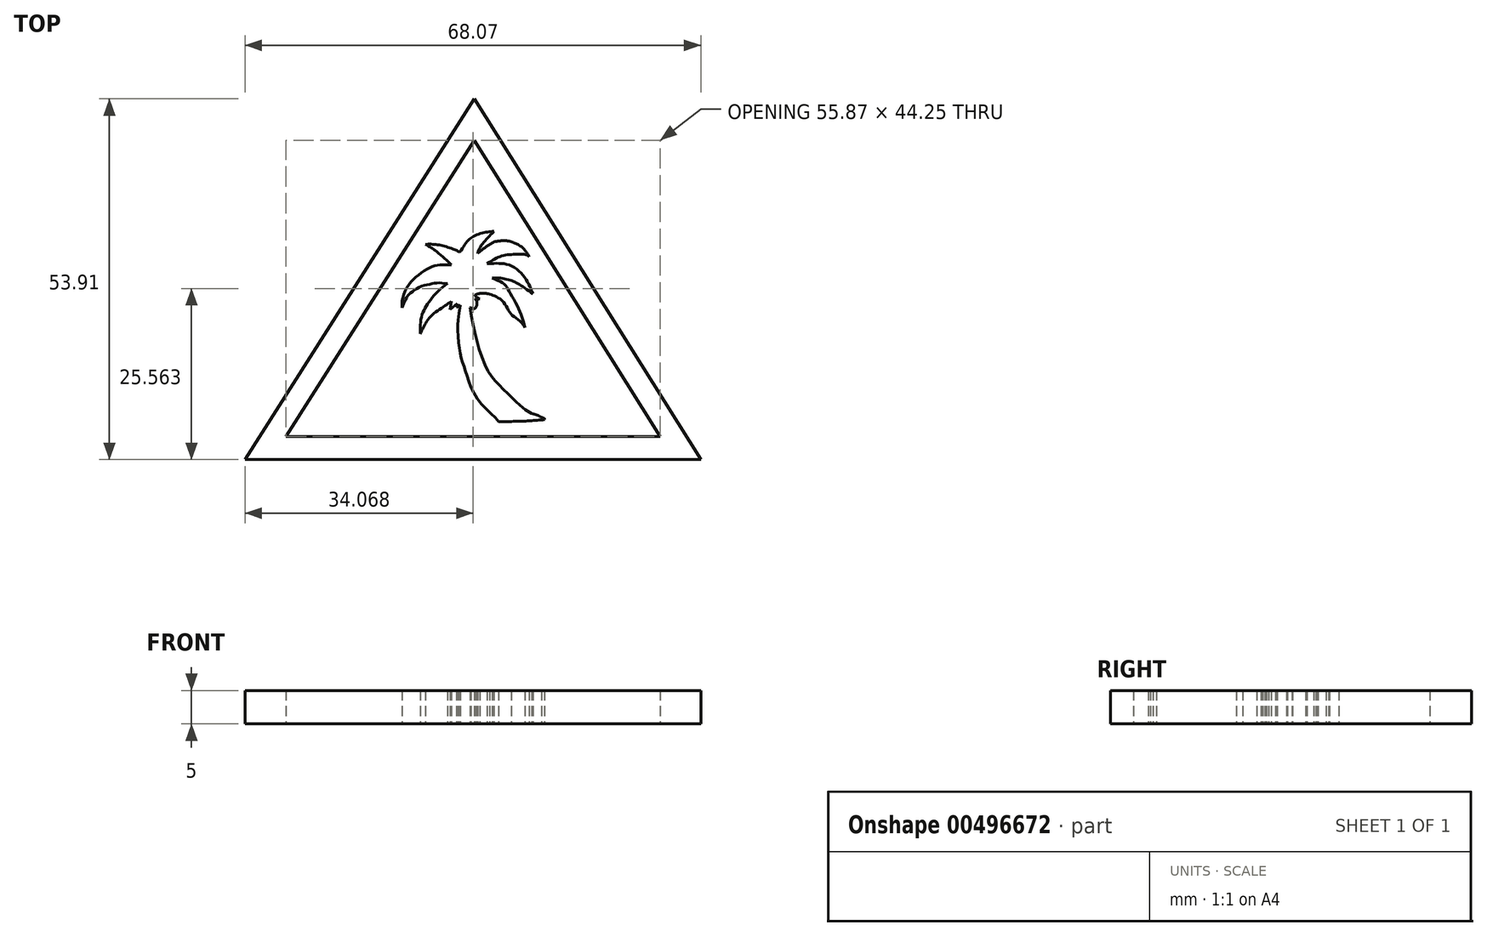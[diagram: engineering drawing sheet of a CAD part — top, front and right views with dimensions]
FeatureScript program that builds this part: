
annotation { "Feature Type Name" : "Feature", "Feature Type Description" : "" }
export const myFeature = defineFeature(function(context is Context, id is Id, definition is map)
    precondition{}
    {
        {
            var Q0;
            Q0=qCreatedBy(makeId("Top.planeOp"),FACE);
            var sketch = newSketch(context, id + "F0", { "sketchPlane" : qUnion([Q0])});
            skLineSegment(sketch, "E0", {"start": v(-38.72, -7.08) * mm, "end": v(-72.96, -61) * mm});
            skLineSegment(sketch, "E1", {"start": v(-72.96, -61) * mm, "end": v(-4.9, -61) * mm});
            skLineSegment(sketch, "E2", {"start": v(-4.9, -61) * mm, "end": v(-38.72, -7.08) * mm});
            skLineSegment(sketch, "E3", {"start": v(-38.72, -13.3) * mm, "end": v(-66.83, -57.55) * mm});
            skLineSegment(sketch, "E4", {"start": v(-66.83, -57.55) * mm, "end": v(-10.96, -57.55) * mm});
            skLineSegment(sketch, "E5", {"start": v(-10.96, -57.55) * mm, "end": v(-38.72, -13.3) * mm});
            skFitSpline(sketch, "E6", {"points": [v(-35.11, -55.3) * mm, v(-31.32, -55.23) * mm, v(-28.22, -55.01) * mm], "startDerivative": vector(7.4, 0.05) * mm, "endDerivative": vector(6.35, 0.54) * mm});
            skFitSpline(sketch, "E7", {"points": [v(-28.22, -55.01) * mm, v(-28.22, -54.88) * mm, v(-28.42, -54.76) * mm, v(-28.66, -54.66) * mm], "startDerivative": vector(0.13, 0.53) * mm, "endDerivative": vector(-0.6, 0.27) * mm});
            skFitSpline(sketch, "E8", {"points": [v(-28.66, -54.66) * mm, v(-29.15, -54.42) * mm, v(-29.59, -54.26) * mm, v(-30.15, -54.1) * mm], "startDerivative": vector(-1.48, 0.76) * mm, "endDerivative": vector(-1.68, 0.48) * mm});
            skFitSpline(sketch, "E9", {"points": [v(-30.15, -54.1) * mm, v(-30.76, -53.73) * mm, v(-31.6, -53.12) * mm, v(-34.28, -50.57) * mm, v(-37.07, -47) * mm, v(-39.14, -39.62) * mm, v(-39.35, -38.29) * mm], "startDerivative": vector(-7.1, 4.24) * mm, "endDerivative": vector(-1.12, 8.32) * mm});
            skFitSpline(sketch, "E10", {"points": [v(-39.35, -38.29) * mm, v(-39.25, -38.22) * mm], "startDerivative": vector(0.1, 0.07) * mm, "endDerivative": vector(0.1, 0.07) * mm});
            skFitSpline(sketch, "E11", {"points": [v(-39.25, -38.22) * mm, v(-39.05, -38.4) * mm, v(-38.8, -38.43) * mm, v(-38.54, -38.29) * mm, v(-38.35, -37.95) * mm, v(-38.33, -37.5) * mm, v(-38.4, -37.24) * mm, v(-38.55, -37.08) * mm, v(-38.55, -37) * mm, v(-38.24, -37) * mm, v(-37.9, -36.97) * mm], "startDerivative": vector(1.92, -2.22) * mm, "endDerivative": vector(2.89, 0.42) * mm});
            skFitSpline(sketch, "E12", {"points": [v(-37.9, -36.97) * mm, v(-38.6, -36.5) * mm, v(-38.62, -36.36) * mm], "startDerivative": vector(-1.33, 0.71) * mm, "endDerivative": vector(0.06, 0.47) * mm});
            skFitSpline(sketch, "E13", {"points": [v(-38.62, -36.36) * mm, v(-38.19, -36.22) * mm, v(-37.53, -36.13) * mm, v(-36.8, -36.18) * mm, v(-36.45, -36.25) * mm], "startDerivative": vector(1.82, 0.64) * mm, "endDerivative": vector(1.56, -0.34) * mm});
            skFitSpline(sketch, "E14", {"points": [v(-36.45, -36.25) * mm, v(-35.77, -36.5) * mm, v(-34.87, -36.98) * mm, v(-34, -37.93) * mm, v(-33.48, -38.95) * mm, v(-32.7, -39.7) * mm, v(-31.68, -40.48) * mm, v(-31.18, -41.25) * mm], "startDerivative": vector(5.54, -2.02) * mm, "endDerivative": vector(3.12, -5.94) * mm});
            skFitSpline(sketch, "E15", {"points": [v(-31.18, -41.25) * mm, v(-31.42, -40.28) * mm, v(-32.26, -38.1) * mm, v(-33.6, -35.68) * mm, v(-34.27, -34.75) * mm, v(-36.05, -33.87) * mm], "startDerivative": vector(-1.3, 5.92) * mm, "endDerivative": vector(-9.79, 3.92) * mm});
            skFitSpline(sketch, "E16", {"points": [v(-36.05, -33.87) * mm, v(-34.72, -33.87) * mm, v(-33.18, -34.24) * mm, v(-32.04, -34.78) * mm, v(-29.98, -36.23) * mm], "startDerivative": vector(5.72, 0.36) * mm, "endDerivative": vector(7.2, -5.3) * mm});
            skFitSpline(sketch, "E17", {"points": [v(-29.98, -36.23) * mm, v(-30.71, -34.56) * mm, v(-31.9, -32.98) * mm, v(-33.61, -31.86) * mm, v(-35.36, -31.66) * mm, v(-36.8, -31.7) * mm], "startDerivative": vector(-3.28, 8.41) * mm, "endDerivative": vector(-7.83, -0.25) * mm});
            skFitSpline(sketch, "E18", {"points": [v(-36.8, -31.7) * mm, v(-35.42, -30.88) * mm, v(-34.16, -30.44) * mm, v(-32.66, -30.31) * mm, v(-31.18, -30.34) * mm, v(-30.52, -30.66) * mm], "startDerivative": vector(6.28, 3.97) * mm, "endDerivative": vector(3.84, -2.53) * mm});
            skFitSpline(sketch, "E19", {"points": [v(-30.52, -30.66) * mm, v(-30.88, -30.06) * mm, v(-31.72, -29.16) * mm, v(-32.79, -28.56) * mm, v(-33.18, -28.44) * mm], "startDerivative": vector(-1.4, 2.53) * mm, "endDerivative": vector(-1.98, 0.53) * mm});
            skFitSpline(sketch, "E20", {"points": [v(-33.18, -28.44) * mm, v(-33.66, -28.31) * mm, v(-34.27, -28.28) * mm, v(-34.8, -28.3) * mm, v(-35.77, -28.44) * mm], "startDerivative": vector(-2.05, 0.68) * mm, "endDerivative": vector(-3.38, -0.57) * mm});
            skFitSpline(sketch, "E21", {"points": [v(-35.77, -28.44) * mm, v(-36.97, -29.2) * mm, v(-38.23, -30.17) * mm], "startDerivative": vector(-2.47, -1.48) * mm, "endDerivative": vector(-2.44, -1.99) * mm});
            skFitSpline(sketch, "E22", {"points": [v(-38.23, -30.17) * mm, v(-37.82, -29.2) * mm, v(-35.77, -26.88) * mm], "startDerivative": vector(0.72, 2.46) * mm, "endDerivative": vector(3.92, 4) * mm});
            skFitSpline(sketch, "E23", {"points": [v(-35.77, -26.88) * mm, v(-37.05, -27.02) * mm, v(-38.6, -27.5) * mm, v(-39.68, -28.3) * mm, v(-40.88, -29.98) * mm], "startDerivative": vector(-5.43, -0.37) * mm, "endDerivative": vector(-4.17, -6.5) * mm});
            skFitSpline(sketch, "E24", {"points": [v(-40.88, -29.98) * mm, v(-41.63, -29.63) * mm, v(-43.15, -29.1) * mm, v(-44.84, -28.82) * mm, v(-46.02, -28.82) * mm], "startDerivative": vector(-3.38, 1.71) * mm, "endDerivative": vector(-4.75, -0.19) * mm});
            skFitSpline(sketch, "E25", {"points": [v(-46.02, -28.82) * mm, v(-44.8, -29.55) * mm, v(-43.82, -30.33) * mm, v(-42.15, -31.86) * mm], "startDerivative": vector(4.1, -2.34) * mm, "endDerivative": vector(4.55, -4.23) * mm});
            skFitSpline(sketch, "E26", {"points": [v(-42.15, -31.86) * mm, v(-43.47, -31.86) * mm, v(-44.58, -32.02) * mm, v(-45.6, -32.43) * mm, v(-47.16, -33.48) * mm, v(-48.46, -34.77) * mm, v(-49.36, -36.6) * mm, v(-49.53, -38.28) * mm], "startDerivative": vector(-10.14, 0.24) * mm, "endDerivative": vector(-0.22, -11.13) * mm});
            skFitSpline(sketch, "E27", {"points": [v(-49.53, -38.28) * mm, v(-49.14, -37.38) * mm, v(-48.66, -36.52) * mm, v(-47.99, -35.9) * mm, v(-46.8, -35.16) * mm, v(-45.35, -34.77) * mm, v(-44.19, -34.58) * mm, v(-42.75, -34.7) * mm], "startDerivative": vector(2.98, 6.86) * mm, "endDerivative": vector(9.47, -1.36) * mm});
            skFitSpline(sketch, "E28", {"points": [v(-42.75, -34.7) * mm, v(-44.26, -35.92) * mm, v(-45.45, -37.37) * mm, v(-46.1, -38.4) * mm, v(-46.6, -39.68) * mm, v(-46.8, -41.08) * mm, v(-46.8, -42.2) * mm], "startDerivative": vector(-8.22, -5.89) * mm, "endDerivative": vector(0.17, -7.43) * mm});
            skFitSpline(sketch, "E29", {"points": [v(-46.8, -42.2) * mm, v(-46.2, -41.03) * mm, v(-45.3, -39.68) * mm, v(-43.56, -38.28) * mm, v(-42.15, -37.37) * mm], "startDerivative": vector(2.56, 5.25) * mm, "endDerivative": vector(5.39, 3.43) * mm});
            skFitSpline(sketch, "E30", {"points": [v(-42.15, -37.37) * mm, v(-42.35, -38.54) * mm], "startDerivative": vector(-0.2, -1.17) * mm, "endDerivative": vector(-0.2, -1.17) * mm});
            skFitSpline(sketch, "E31", {"points": [v(-42.35, -38.54) * mm, v(-41.24, -37.7) * mm], "startDerivative": vector(1.11, 0.84) * mm, "endDerivative": vector(1.11, 0.84) * mm});
            skFitSpline(sketch, "E32", {"points": [v(-41.24, -37.7) * mm, v(-41.41, -38.22) * mm], "startDerivative": vector(-0.18, -0.53) * mm, "endDerivative": vector(-0.18, -0.53) * mm});
            skFitSpline(sketch, "E33", {"points": [v(-41.41, -38.22) * mm, v(-40.84, -37.92) * mm], "startDerivative": vector(0.58, 0.3) * mm, "endDerivative": vector(0.58, 0.3) * mm});
            skFitSpline(sketch, "E34", {"points": [v(-40.84, -37.92) * mm, v(-41, -39.11) * mm], "startDerivative": vector(-0.17, -1.2) * mm, "endDerivative": vector(-0.17, -1.2) * mm});
            skFitSpline(sketch, "E35", {"points": [v(-41, -39.11) * mm, v(-41.17, -40.48) * mm, v(-41.03, -43.79) * mm, v(-40.53, -46.25) * mm, v(-39.8, -48.47) * mm, v(-38.19, -52.05) * mm, v(-35.47, -54.84) * mm, v(-35.11, -55.3) * mm], "startDerivative": vector(-1.93, -10.96) * mm, "endDerivative": vector(3.37, -5.4) * mm});
            skSolve(sketch);
        }
        {
            var Q0;
            Q0 = qSketchRegion(id + "F0", true);
            var Q1;
            Q1=makeQuery(id+"F0.imprint","IMPRINT",FACE,{"disambiguationData":[TD([[makeQuery(id+"F0.imprint","IMPRINT",EDGE,{"derivedFrom":sQuery(id+"F0.wireOp",EDGE,"E6")}),1.0]])]});
            extrude(context, id + "F1", {"entities" : qUnion([Q0, Q1]), "depth" : 5 * mm, "offsetDistance" : 25 * mm});
        }
    });
